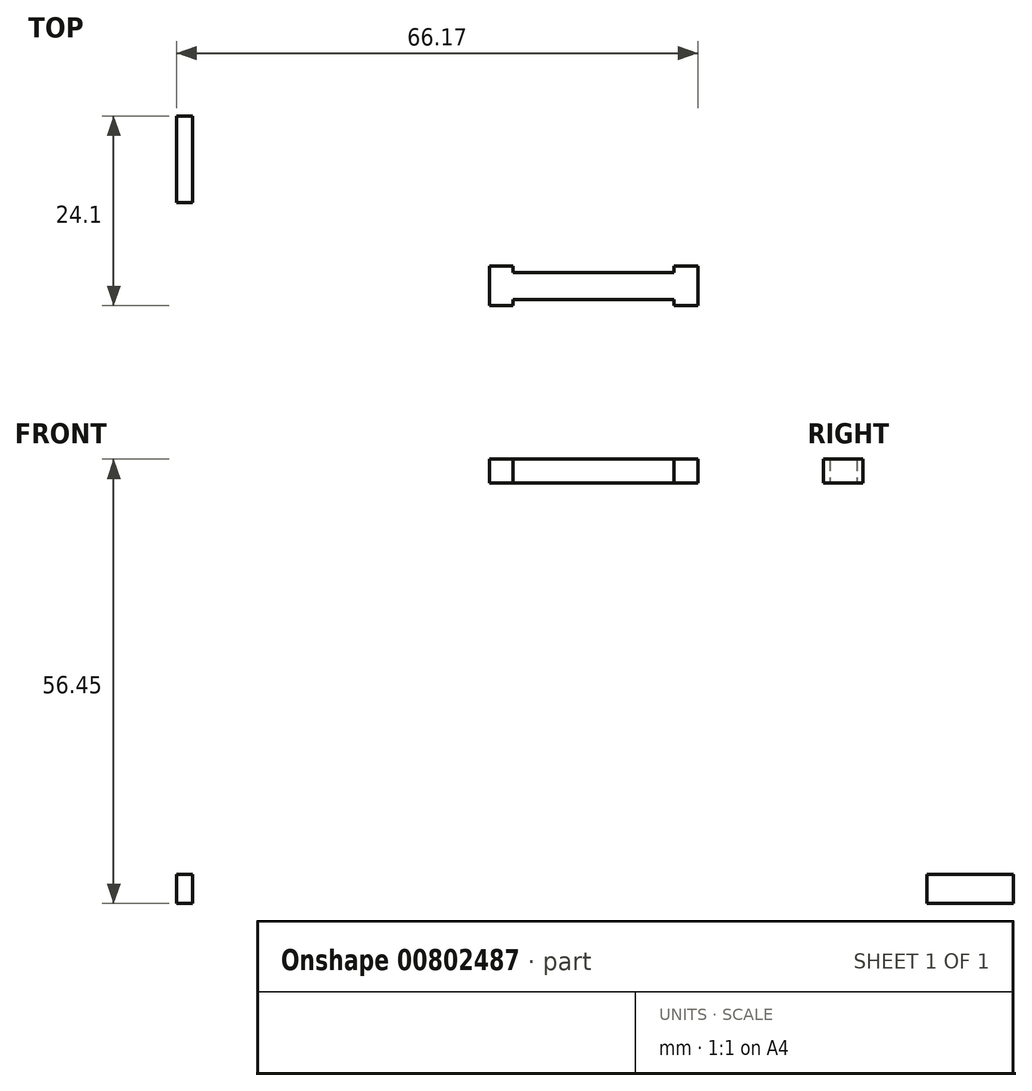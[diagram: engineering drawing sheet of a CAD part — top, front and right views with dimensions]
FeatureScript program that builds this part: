
annotation { "Feature Type Name" : "Feature", "Feature Type Description" : "" }
export const myFeature = defineFeature(function(context is Context, id is Id, definition is map)
    precondition{}
    {
        {
            var Q0;
            Q0=qCreatedBy(makeId("Front.planeOp"),FACE);
            var sketch = newSketch(context, id + "F0", { "sketchPlane" : qUnion([Q0])});
            skPoint(sketch, "E0", {"position": v(-94.69, -57.75) * mm});
            skPoint(sketch, "E1", {"position": v(-94.88, -122.54) * mm});
            skPoint(sketch, "E2", {"position": v(-97.64, -227.46) * mm});
            skPoint(sketch, "E3", {"position": v(-99.64, -52.66) * mm});
            skPoint(sketch, "E3.positionSnap0", {"position": v(-99.64, -48.16) * mm});
            skPoint(sketch, "E4", {"position": v(-99.64, -48.6) * mm});
            skLineSegment(sketch, "E5.bottom", {"start": v(-95.8, -53.45) * mm, "end": v(-93.8, -53.45) * mm});
            skLineSegment(sketch, "E5.top", {"start": v(-95.8, -49.77) * mm, "end": v(-93.8, -49.77) * mm});
            skLineSegment(sketch, "E5.left", {"start": v(-95.8, -53.45) * mm, "end": v(-95.8, -49.77) * mm});
            skLineSegment(sketch, "E5.right", {"start": v(-93.8, -53.45) * mm, "end": v(-93.8, -49.77) * mm});
            skPoint(sketch, "E5.middle", {"position": v(-94.8, -51.6) * mm});
            skLineSegment(sketch, "E6.bottom", {"start": v(-96, -225.36) * mm, "end": v(-94, -225.36) * mm});
            skLineSegment(sketch, "E6.top", {"start": v(-96, -221.76) * mm, "end": v(-94, -221.76) * mm});
            skLineSegment(sketch, "E6.left", {"start": v(-96, -225.36) * mm, "end": v(-96, -221.76) * mm});
            skLineSegment(sketch, "E6.right", {"start": v(-94, -225.36) * mm, "end": v(-94, -221.76) * mm});
            skPoint(sketch, "E6.middle", {"position": v(-95, -223.56) * mm});
            skSolve(sketch);
        }
        {
            var Q0;
            Q0=makeQuery(id+"F0.imprint","IMPRINT",FACE,{"disambiguationData":[TD([[makeQuery(id+"F0.imprint","IMPRINT",EDGE,{"derivedFrom":sQuery(id+"F0.wireOp",EDGE,"E5.bottom")}),1.0]])]});
            extrude(context, id + "F1", {"entities" : qUnion([Q0]), "depth" : 11 * mm, "offsetDistance" : 25 * mm});
        }
        {
            var Q0;
            Q0=qCreatedBy(makeId("Top.planeOp"),FACE);
            var sketch = newSketch(context, id + "F2", { "sketchPlane" : qUnion([Q0])});
            skLineSegment(sketch, "E7.bottom", {"start": v(-32.63, -23.3) * mm, "end": v(-53.1, -23.3) * mm});
            skLineSegment(sketch, "E7.top", {"start": v(-32.63, -19.9) * mm, "end": v(-53.1, -19.9) * mm});
            skPoint(sketch, "E7.middle", {"position": v(-42.87, -21.6) * mm});
            skLineSegment(sketch, "E8.bottom", {"start": v(-29.63, -24.1) * mm, "end": v(-32.63, -24.1) * mm});
            skLineSegment(sketch, "E8.top", {"start": v(-29.63, -19.1) * mm, "end": v(-32.63, -19.1) * mm});
            skLineSegment(sketch, "E8.left", {"start": v(-29.63, -24.1) * mm, "end": v(-29.63, -19.1) * mm});
            skLineSegment(sketch, "E8.right", {"start": v(-32.63, -24.1) * mm, "end": v(-32.63, -23.3) * mm});
            skPoint(sketch, "E8.middle", {"position": v(-31.13, -21.6) * mm});
            skLineSegment(sketch, "E9.bottom", {"start": v(-56.1, -24.1) * mm, "end": v(-53.1, -24.1) * mm});
            skLineSegment(sketch, "E9.top", {"start": v(-56.1, -19.1) * mm, "end": v(-53.1, -19.1) * mm});
            skLineSegment(sketch, "E9.left", {"start": v(-56.1, -24.1) * mm, "end": v(-56.1, -19.1) * mm});
            skLineSegment(sketch, "E9.right", {"start": v(-53.1, -24.1) * mm, "end": v(-53.1, -23.3) * mm});
            skPoint(sketch, "E9.middle", {"position": v(-54.6, -21.6) * mm});
            skPoint(sketch, "E10.orphan", {"position": v(-54.6, -19.9) * mm});
            skPoint(sketch, "E11.orphan", {"position": v(-54.6, -23.3) * mm});
            skPoint(sketch, "E12.orphan", {"position": v(-31.13, -23.3) * mm});
            skPoint(sketch, "E13.orphan", {"position": v(-31.13, -19.9) * mm});
            skLineSegment(sketch, "E14.trimOffspring", {"start": v(-53.1, -19.9) * mm, "end": v(-53.1, -19.1) * mm});
            skLineSegment(sketch, "E15.trimOffspring", {"start": v(-32.63, -19.9) * mm, "end": v(-32.63, -19.1) * mm});
            skSolve(sketch);
        }
        {
            var Q0;
            Q0=makeQuery(id+"F2.imprint","IMPRINT",FACE,{"disambiguationData":[TD([[makeQuery(id+"F2.imprint","IMPRINT",EDGE,{"derivedFrom":sQuery(id+"F2.wireOp",EDGE,"E7.bottom")}),-1.0]])]});
            extrude(context, id + "F3", {"entities" : qUnion([Q0]), "depth" : 3 * mm, "offsetDistance" : 25 * mm});
        }
    });
